# Revit family: Parma 210 LED 2700K
name_source: partatom
category: Lighting Fixtures
revit_build: Autodesk Revit 2018 (Build: 20170223_1515(x64)
units: mm (PartAtom-declared; Revit-internal decimal feet)

## family parameters
Cut with Voids When Loaded = No
Host = Face
Light Source = Yes
OmniClass Number = 23.80.70.00
OmniClass Title = Lighting
Part Type = Normal
Room Calculation Point = No
Round Connector Dimension = Use Diameter
Shared = No

## types (1)
- 8052 Parma 210 LED
    Apparent Load = 8 VA
    Casing Material = Astro - Plaster - Natural
    Class = 1
    Color Filter = 16777215
    Description = Wall Light
    Dimmable = Phase & 1-10V dimming
    Dimming Lamp Color Temperature Shift = <None>
    Heatsink Material = Astro - Aluminium - Anodised
    Height = 210 mm  [stored 0.688976 ft]
    IP Rating = IP20
    Lamp = LED
    Lamp included = Yes
    Length = 110 mm  [stored 0.360892 ft]
    Light Source Elevation = 1600 mm
    Light Source From Wall = 77.5 mm
    Manufacturer = Astro Lighting Ltd, CM20 2DP
    Model = 7273 Parma 210 LED
    Mountable on normally flammable surfaces = Yes
    Number of Poles = 1
    Photometric Web File = GNC-19599  8052 - Parma 210 LED 2700K Phase Dimmable ies.ies
    Product Documentation = http://www.astrolighting.co.uk
    Suitable for bathroom zone = Zone 3
    Tilt Angle = 90.00°
    Type Comments = -Includes integral 1-10v LED dimmable driver
    URL = http://www.astrolighting.co.uk
    Voltage = 230 V
    Wall Bracket Material = Astro - Steel - Chrome Finish
    Wattage Comments = 2x3w
    Weight = 1.72 kg
    Width = 90 mm  [stored 0.295276 ft]

note: [stored X ft] marks values corroborated as IEEE doubles in the binary element streams (Revit-internal decimal feet)

## geometry (parser evidence)
native form markers: Sweep x4
no freeform markers — native parametric forms only
